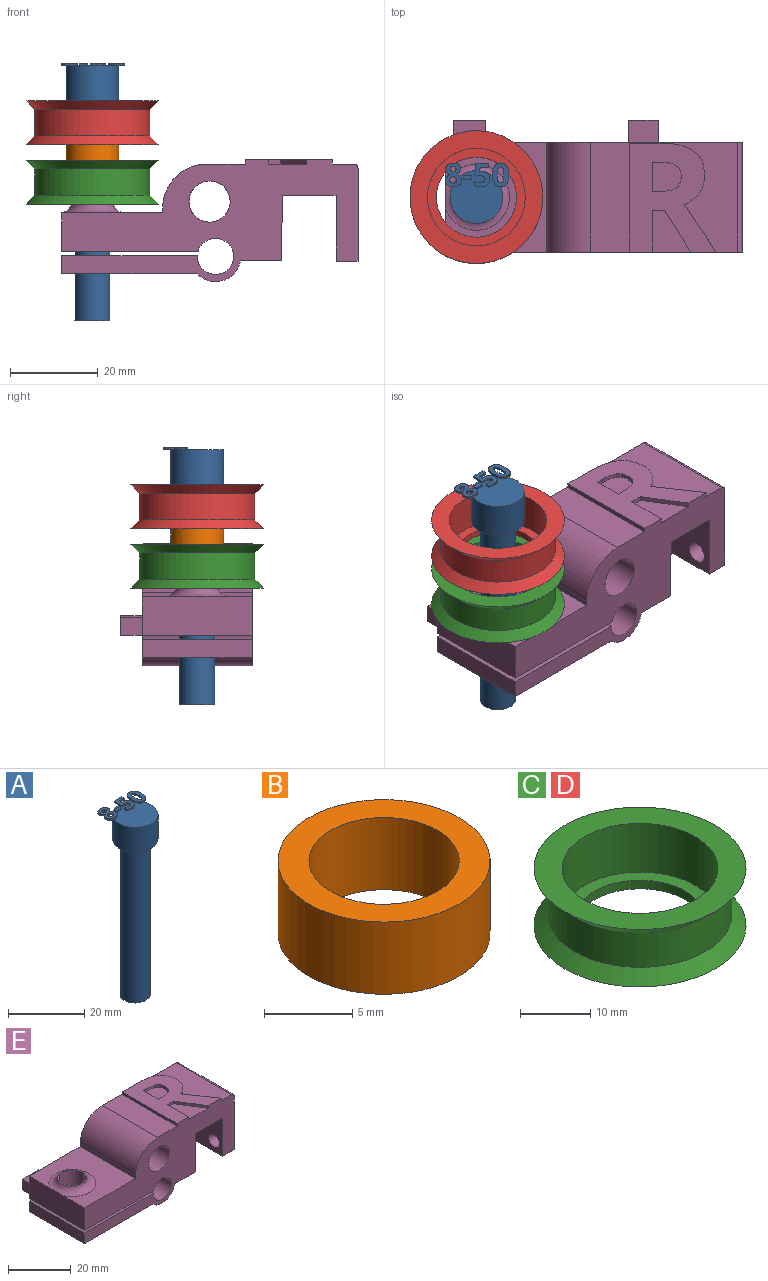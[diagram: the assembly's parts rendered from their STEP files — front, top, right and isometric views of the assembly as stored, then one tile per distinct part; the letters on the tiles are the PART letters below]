
ASSEMBLY  parts=5 mates=4
PART A: 86 faces, bbox 14.5x13.7x58.5 mm
  f0: plane 12x12mm, normal (0,0,1), area 99.4mm2, adj f5,f22,f23,f24,f25,f26,f40,f41
  f1: plane 1x0.26mm, normal (0,0,1), area 0.1mm2, adj f5,f46,f47,f48,f49
  f2: plane 0.85x0.68mm, normal (0,0,1), area 0.2mm2, adj f5,f29,f30,f31
  f3: cylinder r=4mm len=50mm, axis (0,0,-1), area 1256.6mm2, adj f4,f6
  f4: plane 8x8mm, normal (0,0,-1), area 50.3mm2, adj f3
  f5: cylinder r=6mm len=12mm, axis (0,0,-1), area 301.6mm2, adj f0,f1,f2,f6,f39,f45,f67,f85
  f6: plane 12x12mm, normal (0,0,-1), area 62.8mm2, adj f3,f5
  f7: extruded ~0.5x0.46mm, area 0.2mm2, adj f8,f37,f38,f39
  f8: extruded ~0.5x0.46mm, area 0.2mm2, adj f7,f9,f38,f39
  f9: extruded ~0.5x0.39mm, area 0.2mm2, adj f8,f10,f38,f39
  f10: extruded ~0.5x0.4mm, area 0.2mm2, adj f9,f11,f38,f39
  f11: extruded ~0.5x0.49mm, area 0.3mm2, adj f10,f12,f38,f39
  f12: extruded ~0.5x0.5mm, area 0.3mm2, adj f11,f13,f38,f39
  f13: extruded ~0.5x0.39mm, area 0.2mm2, adj f12,f37,f38,f39
  f14: extruded ~1.22x0.5mm, area 0.6mm2, adj f15,f35,f38,f39
  f15: extruded ~1.22x0.5mm, area 0.6mm2, adj f14,f16,f38,f39
  f16: extruded ~0.91x0.5mm, area 0.5mm2, adj f15,f17,f38,f39
  f17: extruded ~0.71x0.5mm, area 0.4mm2, adj f16,f18,f38,f39
  f18: extruded ~0.65x0.61mm, area 0.4mm2, adj f17,f19,f38,f39
  f19: extruded ~0.77x0.62mm, area 0.5mm2, adj f18,f20,f38,f39
  f20: extruded ~0.8x0.5mm, area 0.4mm2, adj f19,f21,f38,f39
  f21: extruded ~1.04x0.5mm, area 0.6mm2, adj f20,f22,f38,f39
  f22: extruded ~1.36x0.5mm, area 0.7mm2, adj f0,f21,f23,f38,f39
  f23: extruded ~1.33x0.5mm, area 0.7mm2, adj f0,f22,f24,f38
  f24: extruded ~1.04x0.51mm, area 0.6mm2, adj f0,f23,f25,f38
  f25: extruded ~0.75x0.5mm, area 0.4mm2, adj f0,f24,f26,f38
  f26: extruded ~0.85x0.66mm, area 0.5mm2, adj f0,f25,f27,f38,f39
  f27: extruded ~0.72x0.56mm, area 0.5mm2, adj f26,f28,f38,f39
  f28: extruded ~0.72x0.5mm, area 0.4mm2, adj f27,f35,f38,f39
  f29: extruded ~0.5x0.45mm, area 0.3mm2, adj f2,f30,f36,f38,f39
  f30: extruded ~0.5x0.47mm, area 0.3mm2, adj f2,f29,f31,f38
  f31: extruded ~0.62x0.5mm, area 0.3mm2, adj f2,f30,f32,f38,f39
  f32: extruded ~0.59x0.5mm, area 0.3mm2, adj f31,f33,f38,f39
  f33: extruded ~0.5x0.48mm, area 0.3mm2, adj f32,f34,f38,f39
  f34: extruded ~0.89x0.77mm, area 0.6mm2, adj f33,f36,f38,f39
  f35: extruded ~0.93x0.5mm, area 0.5mm2, adj f14,f28,f38,f39
  f36: extruded ~0.66x0.5mm, area 0.4mm2, adj f29,f34,f38,f39
  f37: extruded ~0.5x0.39mm, area 0.2mm2, adj f7,f13,f38,f39
  f38: plane 5.4x3.69mm, normal (0,0,1), area 12.7mm2, adj f7,f8,f9,f10,f11,f12,f13,f14
  f39: plane 5.4x3.53mm, normal (0,0,-1), area 10.2mm2, adj f5,f7,f8,f9,f10,f11,f12,f13
  f40: plane 0.9x0.5mm, normal (-1,0,0), area 0.4mm2, adj f0,f41,f43,f44
  f41: plane 1.93x0.5mm, normal (0,-1,0), area 1mm2, adj f0,f40,f42,f44
  f42: plane 0.9x0.5mm, normal (1,0,0), area 0.4mm2, adj f0,f41,f43,f44
  f43: plane 1.93x0.5mm, normal (0,1,0), area 1mm2, adj f0,f40,f42,f44
  f44: plane 1.93x0.9mm, normal (0,0,1), area 1.7mm2, adj f40,f41,f42,f43
  f45: plane 0.76x0.31mm, normal (0,0,-1), area 0mm2, adj f5,f46
  f46: extruded ~1.21x0.5mm, area 0.7mm2, adj f0,f1,f45,f47,f65,f66
  f47: extruded ~0.54x0.5mm, area 0.3mm2, adj f1,f46,f48,f66
  f48: plane 0.5x0.13mm, normal (-0.2,0.98,0), area 0.1mm2, adj f1,f47,f49,f66
  f49: plane 1.03x0.5mm, normal (1,-0.09,0), area 0.5mm2, adj f1,f48,f50,f66,f67
  f50: plane 1.88x0.5mm, normal (0,-1,0), area 0.9mm2, adj f49,f51,f66,f67
  f51: plane 0.94x0.5mm, normal (1,0,0), area 0.5mm2, adj f50,f52,f66,f67
  f52: plane 2.85x0.5mm, normal (0,1,0), area 1.4mm2, adj f51,f53,f66,f67
  f53: plane 2.68x0.5mm, normal (-1,0.07,0), area 1.3mm2, adj f0,f52,f54,f66,f67
  f54: plane 0.5x0.44mm, normal (-0.47,-0.88,0), area 0.3mm2, adj f0,f53,f55,f66
  f55: extruded ~0.5x0.37mm, area 0.2mm2, adj f0,f54,f56,f66
  f56: extruded ~0.5x0.42mm, area 0.2mm2, adj f0,f55,f57,f66
  f57: extruded ~1.05x0.8mm, area 0.8mm2, adj f0,f56,f58,f66
  f58: extruded ~1.02x0.83mm, area 0.8mm2, adj f0,f57,f59,f66
  f59: extruded ~0.72x0.5mm, area 0.4mm2, adj f0,f58,f60,f66
  f60: extruded ~0.66x0.5mm, area 0.4mm2, adj f0,f59,f61,f66
  f61: plane 0.96x0.5mm, normal (-1,0,0), area 0.5mm2, adj f0,f60,f62,f66
  f62: extruded ~1.42x0.5mm, area 0.7mm2, adj f0,f61,f63,f66
  f63: extruded ~1.55x0.5mm, area 0.8mm2, adj f0,f62,f64,f66
  f64: extruded ~1.36x0.54mm, area 0.8mm2, adj f0,f63,f65,f66
  f65: extruded ~1.17x0.5mm, area 0.6mm2, adj f0,f46,f64,f66
  f66: plane 5.33x3.51mm, normal (0,0,1), area 10.9mm2, adj f46,f47,f48,f49,f50,f51,f52,f53
  f67: plane 2.97x1.71mm, normal (0,0,-1), area 3.5mm2, adj f5,f49,f50,f51,f52,f53
  f68: extruded ~1.39x0.5mm, area 0.7mm2, adj f69,f83,f84,f85
  f69: extruded ~1.39x0.5mm, area 0.7mm2, adj f68,f70,f84,f85
  f70: extruded ~0.56x0.5mm, area 0.4mm2, adj f69,f71,f84,f85
  f71: extruded ~0.56x0.5mm, area 0.4mm2, adj f70,f72,f84,f85
  f72: extruded ~1.39x0.5mm, area 0.7mm2, adj f71,f73,f84,f85
  f73: extruded ~1.38x0.5mm, area 0.7mm2, adj f72,f74,f84,f85
  f74: extruded ~0.56x0.5mm, area 0.4mm2, adj f73,f83,f84,f85
  f75: extruded ~2.04x0.5mm, area 1.1mm2, adj f76,f82,f84,f85
  f76: extruded ~2.02x0.5mm, area 1.1mm2, adj f75,f77,f84,f85
  f77: extruded ~1.38x0.69mm, area 0.8mm2, adj f76,f78,f84,f85
  f78: extruded ~1.38x0.66mm, area 0.8mm2, adj f77,f79,f84,f85
  f79: extruded ~2.05x0.5mm, area 1.1mm2, adj f78,f80,f84,f85
  f80: extruded ~2.02x0.5mm, area 1mm2, adj f0,f79,f81,f84,f85
  f81: extruded ~1.37x0.68mm, area 0.8mm2, adj f0,f80,f82,f84
  f82: extruded ~1.39x0.66mm, area 0.8mm2, adj f0,f75,f81,f84,f85
  f83: extruded ~0.56x0.5mm, area 0.4mm2, adj f68,f74,f84,f85
  f84: plane 5.41x3.68mm, normal (0,0,1), area 12.1mm2, adj f68,f69,f70,f71,f72,f73,f74,f75
  f85: plane 5.41x3.68mm, normal (0,0,-1), area 10.3mm2, adj f5,f68,f69,f70,f71,f72,f73,f74
PART B: 4 faces, bbox 12x12x5 mm
  f0: cylinder r=4.25mm len=8.5mm, axis (0,0,-1), area 133.5mm2, adj f2,f3
  f1: cylinder r=6mm len=12mm, axis (0,0,-1), area 188.5mm2, adj f2,f3
  f2: plane 12x12mm, normal (0,0,1), area 56.4mm2, adj f0,f1
  f3: plane 12x12mm, normal (0,0,-1), area 56.4mm2, adj f0,f1
PART C: 8 faces, bbox 30.2x30.2x10 mm
  f0: plane 30.2x30.2mm, normal (0,0,1), area 329.2mm2, adj f1,f7
  f1: cylinder r=11.1mm len=22.2mm, axis (0,0,-1), area 592.8mm2, adj f0,f2
  f2: plane 22.2x22.2mm, normal (0,0,1), area 126.9mm2, adj f1,f3
  f3: cylinder r=9.1mm len=18.2mm, axis (0,0,-1), area 85.8mm2, adj f2,f4
  f4: plane 30.2x30.2mm, normal (0,0,-1), area 456.2mm2, adj f3,f5
  f5: cone r=13.1mm half-angle=45deg, axis (0,0,-1), area 250.6mm2, adj f4,f6
  f6: cylinder r=13.1mm len=26.2mm, axis (0,0,-1), area 493.9mm2, adj f5,f7
  f7: cone r=15.1mm half-angle=45deg, axis (0,0,1), area 250.6mm2, adj f0,f6
PART D: same geometry as C
PART E: 56 faces, bbox 70.9x30x27.7 mm
  f0: plane 33.42x25mm, normal (0,0,1), area 442.1mm2, adj f14,f15,f25,f27,f40,f41,f42,f43
  f1: plane 9.51x8.71mm, normal (0,0,1), area 54.7mm2, adj f14,f37,f38,f39
  f2: plane 25x4.12mm, normal (-1,0,0), area 103mm2, adj f5,f14,f15,f19
  f3: cylinder r=4.17mm len=8.35mm, axis (0,0,1), area 108.1mm2, adj f5,f19
  f4: plane 25x9.34mm, normal (0,0,-1), area 233.4mm2, adj f13,f14,f15,f17
  f5: plane 30.88x25mm, normal (0,0,-1), area 717.2mm2, adj f2,f3,f14,f15,f17
  f6: plane 25x8.82mm, normal (-1,0,0), area 219.6mm2, adj f7,f14,f15,f20,f24
  f7: plane 25x23mm, normal (0,0,1), area 400mm2, adj f6,f8,f14,f15,f24
  f8: plane 25x1.1mm, normal (-1,0,0), area 27.5mm2, adj f7,f14,f15,f25
  f9: plane 25x21.09mm, normal (1,0,0), area 493.5mm2, adj f10,f14,f15,f22,f23,f27
  f10: plane 25x5mm, normal (0,0,-1), area 125mm2, adj f9,f11,f14,f15
  f11: plane 25x15mm, normal (-1,0,0), area 341.3mm2, adj f10,f12,f14,f15,f22,f23
  f12: plane 25x12.2mm, normal (0,0,-1), area 305mm2, adj f11,f13,f14,f15
  f13: plane 25x14.91mm, normal (1,0,-0.01), area 372.8mm2, adj f4,f12,f14,f15
  f14: plane 67.42x27.75mm, normal (0,-1,0), area 1012mm2, adj f0,f1,f2,f4,f5,f6,f7,f8
  f15: plane 67.42x26.75mm, normal (0,1,0), area 941mm2, adj f0,f2,f4,f5,f6,f7,f8,f9
  f16: cylinder r=4.17mm len=10.78mm, axis (0,0,1), area 282.8mm2, adj f20,f21
  f17: cylinder r=5.75mm len=25mm, axis (0,-1,0), area 315.9mm2, adj f4,f5,f14,f15
  f18: cylinder r=4.1mm len=25mm, axis (0,-1,0), area 618.7mm2, adj f14,f15,f19,f20
  f19: plane 30.91x25mm, normal (0,0,1), area 718.1mm2, adj f2,f3,f14,f15,f18
  f20: plane 31.07x30mm, normal (0,0,-1), area 758.4mm2, adj f6,f14,f15,f16,f18,f29,f30,f31
  f21: plane 9.35x9.35mm, normal (0,0,1), area 13.9mm2, adj f16,f24
  f22: cylinder r=2.43mm len=5mm, axis (1,0,0), area 76.2mm2, adj f9,f11
  f23: cylinder r=2.2mm len=5mm, axis (1,0,0), area 69.1mm2, adj f9,f11
  f24: torus R=7.5mm, axis (0,0,-1), area 134.6mm2, adj f6,f7,f21
  f25: cylinder r=10mm len=25mm, axis (0,-1,0), area 392.7mm2, adj f0,f8,f14,f15
  f26: cylinder r=4.68mm len=25mm, axis (0,-1,0), area 735.2mm2, adj f14,f15
  f27: cylinder r=1mm len=25mm, axis (0,-1,0), area 39.3mm2, adj f0,f9,f14,f15
  f28: plane 7.3x5mm, normal (0,0,1), area 36.5mm2, adj f15,f29,f30,f31
  f29: plane 5x4.12mm, normal (-1,0,0), area 20.6mm2, adj f15,f20,f28,f31
  f30: plane 5x4.12mm, normal (1,0,0), area 20.6mm2, adj f15,f20,f28,f31
  f31: plane 7.3x4.12mm, normal (0,1,0), area 30.1mm2, adj f20,f28,f29,f30
  f32: plane 6.63x5mm, normal (0,0,1), area 33.2mm2, adj f15,f33,f35,f36
  f33: plane 5x4.5mm, normal (-1,0,0), area 22.5mm2, adj f15,f32,f34,f36
  f34: plane 6.63x5mm, normal (0,0,-1), area 33.2mm2, adj f15,f33,f35,f36
  f35: plane 5x4.5mm, normal (1,0,0), area 22.5mm2, adj f15,f32,f34,f36
  f36: plane 6.63x4.5mm, normal (0,1,0), area 29.9mm2, adj f32,f33,f34,f35
  f37: plane 9.51x1mm, normal (1,0,0), area 9.5mm2, adj f1,f14,f38,f54
  f38: plane 2.79x1mm, normal (0,-1,0), area 2.8mm2, adj f1,f37,f39,f54
  f39: plane 9.51x5.92mm, normal (-0.85,-0.53,0), area 11.2mm2, adj f1,f14,f38,f54
  f40: extruded ~10.8x7.29mm, area 13mm2, adj f0,f14,f41,f54
  f41: extruded ~3.41x2.67mm, area 4.4mm2, adj f0,f40,f42,f54
  f42: extruded ~3.89x1.2mm, area 4.1mm2, adj f0,f41,f43,f54
  f43: extruded ~5.59x2.42mm, area 6.3mm2, adj f0,f42,f44,f54
  f44: extruded ~7.48x1.84mm, area 7.8mm2, adj f0,f43,f45,f54
  f45: plane 7.22x1mm, normal (0,1,0), area 7.2mm2, adj f0,f44,f46,f54
  f46: plane 24.79x1mm, normal (-1,0,0), area 24.8mm2, adj f0,f14,f45,f54
  f47: plane 1.69x1mm, normal (0,1,0), area 1.7mm2, adj f48,f53,f54,f55
  f48: plane 6.7x1mm, normal (1,0,0), area 6.7mm2, adj f47,f49,f54,f55
  f49: plane 1.6x1mm, normal (0,-1,0), area 1.6mm2, adj f48,f50,f54,f55
  f50: extruded ~3.75x1mm, area 3.9mm2, adj f49,f51,f54,f55
  f51: extruded ~2.51x1.21mm, area 2.9mm2, adj f50,f52,f54,f55
  f52: extruded ~2.61x1.19mm, area 3mm2, adj f51,f53,f54,f55
  f53: extruded ~3.68x1mm, area 3.8mm2, adj f47,f52,f54,f55
  f54: plane 24.79x19.8mm, normal (0,0,1), area 300mm2, adj f14,f37,f38,f39,f40,f41,f42,f43
  f55: plane 6.7x6.56mm, normal (0,0,1), area 38.8mm2, adj f47,f48,f49,f50,f51,f52,f53
PLACE A t=(-103.78,-12.5,-13.6)mm
PLACE B rot(axis=(1,0,0),180deg) t=(-103.78,-12.5,26.4)mm
PLACE C t=(-103.78,-12.5,18.1)mm
PLACE D t=(-103.78,-12.5,31.6)mm
PLACE E at identity
MATE fastened A.f3 <-> D.f1  axis (0,0,-1) through (-103.78,-12.5,36.4)mm
MATE fastened B.f0 <-> C.f1  axis (0,0,1) through (-103.78,-12.5,21.4)mm
MATE fastened C.f1 <-> E.f3  axis (0,0,-1) through (-103.78,-12.5,12.9)mm
MATE fastened D.f1 <-> B.f0  axis (0,0,-1) through (-103.78,-12.5,26.4)mm
